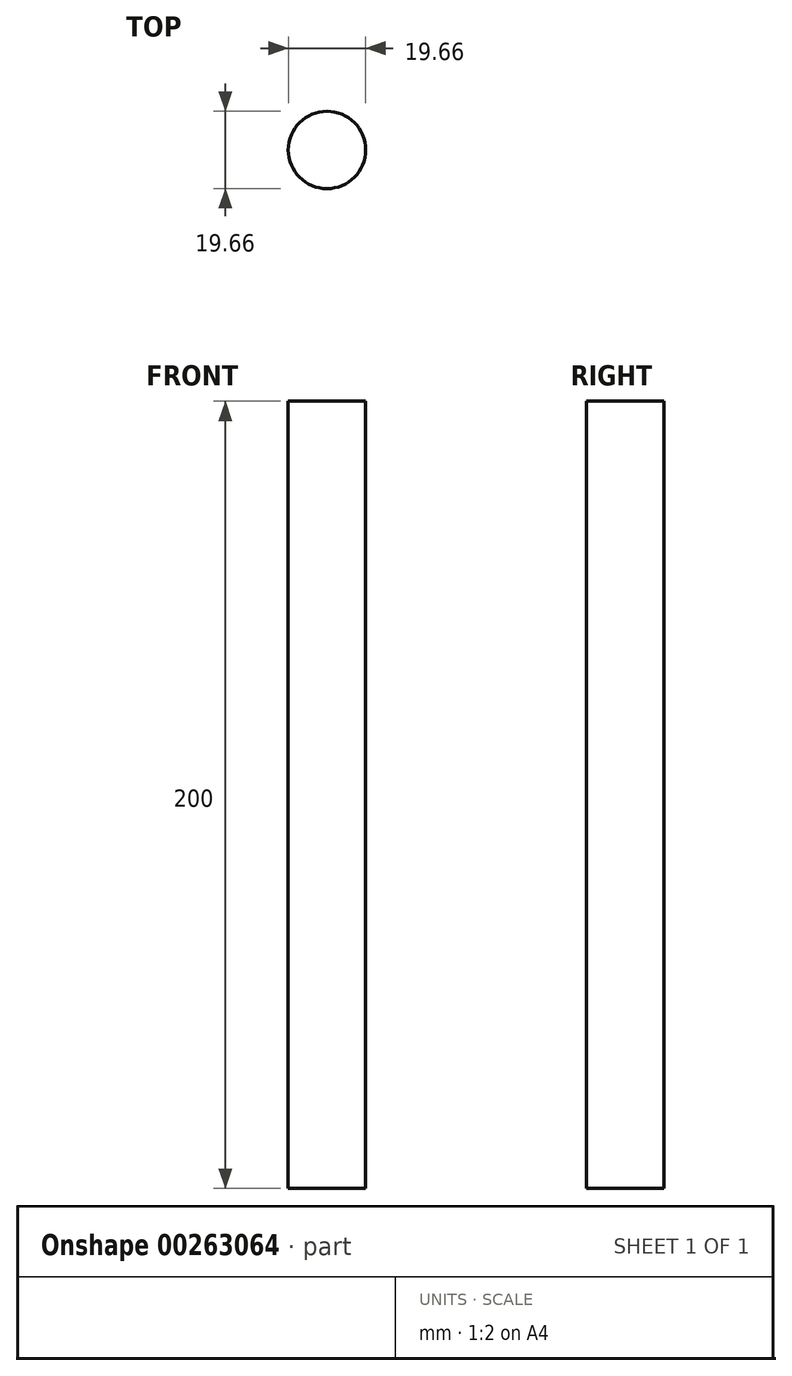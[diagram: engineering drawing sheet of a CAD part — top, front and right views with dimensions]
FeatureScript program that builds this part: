
annotation { "Feature Type Name" : "Feature", "Feature Type Description" : "" }
export const myFeature = defineFeature(function(context is Context, id is Id, definition is map)
    precondition{}
    {
        {
            var Q0;
            Q0=qCreatedBy(makeId("Top.planeOp"),FACE);
            var sketch = newSketch(context, id + "F0", { "sketchPlane" : qUnion([Q0])});
            skCircle(sketch, "E0", {"center": v(0, 0) * mm, "radius": 9.83 * mm});
            skPoint(sketch, "E1", {"position": v(-64.32, 21.3) * mm});
            skPoint(sketch, "E2", {"position": v(-11.78, -31.03) * mm});
            skSolve(sketch);
        }
        {
            var Q0;
            Q0=makeQuery(id+"F0.imprint","IMPRINT",FACE,{"disambiguationData":[TD([[makeQuery(id+"F0.imprint","IMPRINT",EDGE,{"derivedFrom":sQuery(id+"F0.wireOp",EDGE,"E0")}),1.0]])]});
            extrude(context, id + "F1", {"entities" : qUnion([Q0]), "depth" : 200 * mm});
        }
    });
